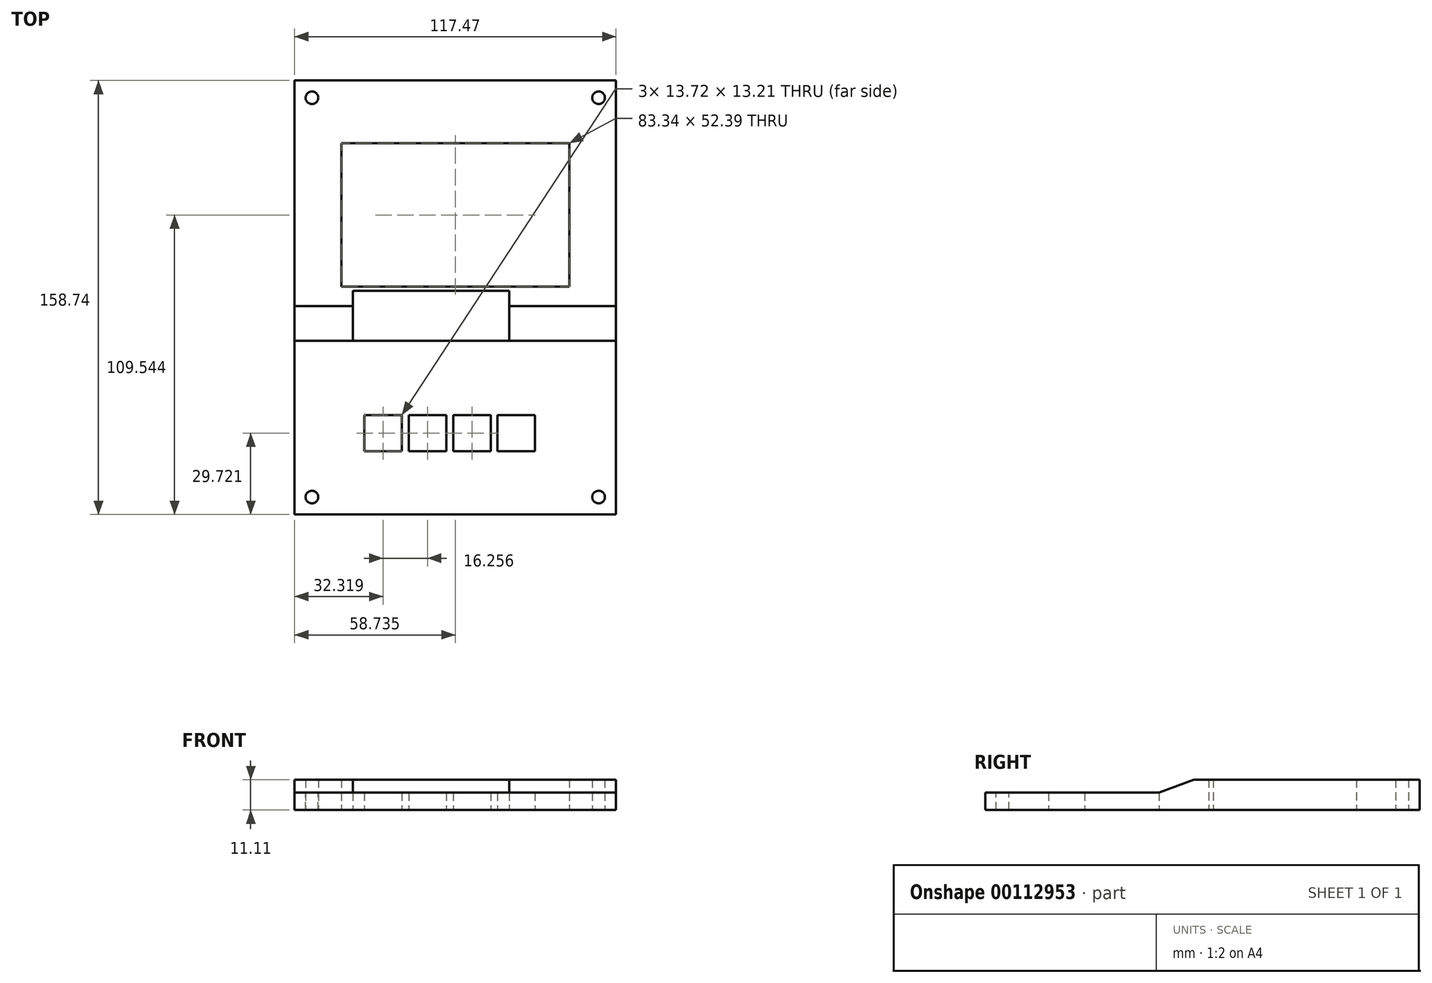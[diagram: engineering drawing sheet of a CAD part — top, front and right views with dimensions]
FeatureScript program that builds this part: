
annotation { "Feature Type Name" : "Feature", "Feature Type Description" : "" }
export const myFeature = defineFeature(function(context is Context, id is Id, definition is map)
    precondition{}
    {
        {
            var Q0;
            Q0=qCreatedBy(makeId("Top.planeOp"),FACE);
            var sketch = newSketch(context, id + "F0", { "sketchPlane" : qUnion([Q0])});
            skLineSegment(sketch, "E0.bottom", {"start": v(-61.75, 43.05) * mm, "end": v(30.32, 43.05) * mm});
            skLineSegment(sketch, "E0.top", {"start": v(-61.75, -26.8) * mm, "end": v(30.32, -26.8) * mm});
            skLineSegment(sketch, "E0.left", {"start": v(-61.75, 43.05) * mm, "end": v(-61.75, -26.8) * mm});
            skLineSegment(sketch, "E0.right", {"start": v(30.32, 43.05) * mm, "end": v(30.32, -26.8) * mm});
            skLineSegment(sketch, "E1", {"start": v(30.32, 43.05) * mm, "end": v(43.02, 43.05) * mm});
            skLineSegment(sketch, "E2", {"start": v(43.02, 43.05) * mm, "end": v(43.02, -26.8) * mm});
            skLineSegment(sketch, "E3", {"start": v(43.02, -26.8) * mm, "end": v(30.32, -26.8) * mm});
            skLineSegment(sketch, "E4", {"start": v(-61.75, 43.05) * mm, "end": v(-74.45, 43.05) * mm});
            skLineSegment(sketch, "E5", {"start": v(-74.45, 43.05) * mm, "end": v(-74.45, -26.8) * mm});
            skLineSegment(sketch, "E6", {"start": v(-74.45, -26.8) * mm, "end": v(-61.75, -26.8) * mm});
            skLineSegment(sketch, "E7", {"start": v(-74.45, 43.05) * mm, "end": v(-74.45, 55.73) * mm});
            skLineSegment(sketch, "E8", {"start": v(-74.45, 55.73) * mm, "end": v(43.02, 55.73) * mm});
            skLineSegment(sketch, "E9", {"start": v(43.02, 55.73) * mm, "end": v(43.02, 43.05) * mm});
            skLineSegment(sketch, "E10", {"start": v(-74.45, 55.73) * mm, "end": v(-68.1, 55.73) * mm});
            skLineSegment(sketch, "E11", {"start": v(-74.45, 55.73) * mm, "end": v(-74.45, 49.39) * mm});
            skCircle(sketch, "E12", {"center": v(-68.1, 49.39) * mm, "radius": 2.31 * mm});
            skLineSegment(sketch, "E13", {"start": v(43.02, 55.73) * mm, "end": v(36.67, 55.73) * mm});
            skLineSegment(sketch, "E14", {"start": v(36.67, 55.73) * mm, "end": v(43.02, 55.73) * mm});
            skCircle(sketch, "E15", {"center": v(36.67, 49.39) * mm, "radius": 2.31 * mm});
            skSolve(sketch);
        }
        {
            var Q0;
            Q0=makeQuery(id+"F0.imprint","IMPRINT",FACE,{"disambiguationData":[TD([[makeQuery(id+"F0.imprint","IMPRINT",EDGE,{"derivedFrom":sQuery(id+"F0.wireOp",EDGE,"E0.bottom")}),-1.0]])]});
            extrude(context, id + "F1", {"entities" : qUnion([Q0]), "depth" : 11.1 * mm});
        }
        {
            var Q0;
            Q0=makeQuery(id+"F1.opExtrude","CAP_FACE",FACE,{"disambiguationData":[OSD([sQuery(id+"F0.wireOp",EDGE,"E0.bottom"),sQuery(id+"F0.wireOp",EDGE,"E0.top"),sQuery(id+"F0.wireOp",EDGE,"E0.left"),sQuery(id+"F0.wireOp",EDGE,"E0.right")])],"isStart":true});
            var sketch = newSketch(context, id + "F2", { "sketchPlane" : qUnion([Q0])});
            skLineSegment(sketch, "E16.0.0", {"start": v(-35.27, 79.9) * mm, "end": v(-35.27, 71.25) * mm});
            skLineSegment(sketch, "E16.0.2", {"start": v(-48.99, 71.25) * mm, "end": v(-48.99, 79.9) * mm});
            skLineSegment(sketch, "E17.0.0", {"start": v(-19.02, 79.9) * mm, "end": v(-19.02, 71.25) * mm});
            skLineSegment(sketch, "E17.0.2", {"start": v(-32.73, 71.25) * mm, "end": v(-32.73, 79.9) * mm});
            skLineSegment(sketch, "E18.0.0", {"start": v(-2.76, 79.9) * mm, "end": v(-2.76, 71.25) * mm});
            skLineSegment(sketch, "E18.0.2", {"start": v(-16.48, 71.25) * mm, "end": v(-16.48, 79.9) * mm});
            skLineSegment(sketch, "E19.0.0", {"start": v(13.37, 79.9) * mm, "end": v(13.37, 71.25) * mm});
            skLineSegment(sketch, "E19.0.2", {"start": v(-0.35, 71.25) * mm, "end": v(-0.35, 79.9) * mm});
            skLineSegment(sketch, "E20.0.0", {"start": v(14.05, 39.5) * mm, "end": v(-61.75, 39.5) * mm});
            skLineSegment(sketch, "E20.0.1", {"start": v(-61.75, 39.5) * mm, "end": v(-61.75, 90.3) * mm});
            skLineSegment(sketch, "E20.0.2", {"start": v(-61.75, 90.3) * mm, "end": v(30.32, 90.3) * mm});
            skLineSegment(sketch, "E20.0.3", {"start": v(30.32, 90.3) * mm, "end": v(34.13, 81.24) * mm});
            skLineSegment(sketch, "E20.0.4", {"start": v(34.13, 81.24) * mm, "end": v(34.13, 39.5) * mm});
            skLineSegment(sketch, "E20.0.5", {"start": v(34.13, 39.5) * mm, "end": v(14.05, 39.5) * mm});
            skLineSegment(sketch, "E21.0.0", {"start": v(-49.05, 26.8) * mm, "end": v(-61.75, 26.8) * mm});
            skLineSegment(sketch, "E21.0.1", {"start": v(-61.75, 26.8) * mm, "end": v(-61.75, 39.5) * mm});
            skLineSegment(sketch, "E21.0.2", {"start": v(-61.75, 39.5) * mm, "end": v(14.05, 39.5) * mm});
            skLineSegment(sketch, "E21.0.3", {"start": v(14.05, 39.5) * mm, "end": v(34.13, 39.5) * mm});
            skLineSegment(sketch, "E21.0.4", {"start": v(34.13, 39.5) * mm, "end": v(34.13, 26.8) * mm});
            skLineSegment(sketch, "E21.0.5", {"start": v(34.13, 26.8) * mm, "end": v(27.78, 26.8) * mm});
            skLineSegment(sketch, "E21.0.6", {"start": v(27.78, 26.8) * mm, "end": v(3.96, 26.8) * mm});
            skLineSegment(sketch, "E21.0.7", {"start": v(3.96, 26.8) * mm, "end": v(-49.05, 26.8) * mm});
            skLineSegment(sketch, "E22.0.2", {"start": v(3.96, 26.8) * mm, "end": v(3.96, 21.25) * mm});
            skLineSegment(sketch, "E22.0.3", {"start": v(3.96, 21.25) * mm, "end": v(-45.24, 21.25) * mm});
            skLineSegment(sketch, "E23.0.0", {"start": v(23.97, -32.73) * mm, "end": v(-55.4, -32.73) * mm});
            skLineSegment(sketch, "E23.0.2", {"start": v(-55.4, 19.66) * mm, "end": v(23.97, 19.66) * mm});
            skLineSegment(sketch, "E24", {"start": v(3.96, 26.8) * mm, "end": v(3.96, 39.5) * mm});
            skLineSegment(sketch, "E25", {"start": v(-61.75, 90.3) * mm, "end": v(-61.75, 103) * mm});
            skLineSegment(sketch, "E26", {"start": v(30.32, 103) * mm, "end": v(30.32, 90.3) * mm});
            skLineSegment(sketch, "E27", {"start": v(-61.75, 103) * mm, "end": v(30.32, 103) * mm});
            skLineSegment(sketch, "E28", {"start": v(-57.38, -32.73) * mm, "end": v(25.95, -32.73) * mm});
            skLineSegment(sketch, "E29", {"start": v(-53.2, 26.8) * mm, "end": v(-53.2, 21.25) * mm});
            skLineSegment(sketch, "E30", {"start": v(-45.24, 21.25) * mm, "end": v(-53.2, 21.25) * mm});
            skLineSegment(sketch, "E31", {"start": v(-53.2, 26.8) * mm, "end": v(-53.2, 39.5) * mm});
            skLineSegment(sketch, "E32", {"start": v(-57.38, -32.73) * mm, "end": v(-57.38, 19.66) * mm});
            skLineSegment(sketch, "E33", {"start": v(-57.38, 19.66) * mm, "end": v(-55.4, 19.66) * mm});
            skLineSegment(sketch, "E34", {"start": v(25.95, -32.73) * mm, "end": v(25.95, 19.66) * mm});
            skLineSegment(sketch, "E35", {"start": v(25.95, 19.66) * mm, "end": v(23.97, 19.66) * mm});
            skLineSegment(sketch, "E36", {"start": v(24.63, 103) * mm, "end": v(24.63, 66.68) * mm});
            skLineSegment(sketch, "E37.bottom", {"start": v(-0.35, 66.68) * mm, "end": v(13.37, 66.68) * mm});
            skLineSegment(sketch, "E37.left", {"start": v(-0.35, 66.68) * mm, "end": v(-0.35, 79.9) * mm});
            skLineSegment(sketch, "E37.right", {"start": v(13.37, 66.68) * mm, "end": v(13.37, 79.9) * mm});
            skLineSegment(sketch, "E38.bottom", {"start": v(-16.48, 66.68) * mm, "end": v(-2.76, 66.68) * mm});
            skLineSegment(sketch, "E38.top", {"start": v(-16.48, 79.9) * mm, "end": v(-2.76, 79.9) * mm});
            skLineSegment(sketch, "E38.left", {"start": v(-16.48, 66.68) * mm, "end": v(-16.48, 79.9) * mm});
            skLineSegment(sketch, "E38.right", {"start": v(-2.76, 66.68) * mm, "end": v(-2.76, 79.9) * mm});
            skLineSegment(sketch, "E39.bottom", {"start": v(-32.73, 66.68) * mm, "end": v(-19.02, 66.68) * mm});
            skLineSegment(sketch, "E39.top", {"start": v(-32.73, 79.9) * mm, "end": v(-19.02, 79.9) * mm});
            skLineSegment(sketch, "E39.left", {"start": v(-32.73, 66.68) * mm, "end": v(-32.73, 79.9) * mm});
            skLineSegment(sketch, "E39.right", {"start": v(-19.02, 66.68) * mm, "end": v(-19.02, 79.9) * mm});
            skLineSegment(sketch, "E40.bottom", {"start": v(-48.99, 66.68) * mm, "end": v(-35.27, 66.68) * mm});
            skLineSegment(sketch, "E40.top", {"start": v(-48.99, 79.9) * mm, "end": v(-35.27, 79.9) * mm});
            skLineSegment(sketch, "E40.left", {"start": v(-48.99, 66.68) * mm, "end": v(-48.99, 79.9) * mm});
            skLineSegment(sketch, "E40.right", {"start": v(-35.27, 66.68) * mm, "end": v(-35.27, 79.9) * mm});
            skPoint(sketch, "E41.orphan", {"position": v(-35.27, 84.46) * mm});
            skPoint(sketch, "E42.orphan", {"position": v(-0.35, 84.46) * mm});
            skPoint(sketch, "E43.orphan", {"position": v(-2.76, 84.46) * mm});
            skPoint(sketch, "E44.orphan", {"position": v(13.37, 81.24) * mm});
            skLineSegment(sketch, "E45", {"start": v(-0.35, 79.9) * mm, "end": v(13.37, 79.9) * mm});
            skPoint(sketch, "E46.orphan", {"position": v(-48.99, 84.46) * mm});
            skLineSegment(sketch, "E47", {"start": v(-57.38, 21.28) * mm, "end": v(-53.2, 21.25) * mm});
            skSolve(sketch);
        }
        {
            var Q0;
            Q0=makeQuery(id+"F1.opExtrude","SWEPT_FACE",FACE,{"disambiguationData":[OSD([sQuery(id+"F0.wireOp",EDGE,"E0.left")])]});
            var sketch = newSketch(context, id + "F3", { "sketchPlane" : qUnion([Q0])});
            skLineSegment(sketch, "E48", {"start": v(26.8, 11.11) * mm, "end": v(26.8, 0) * mm});
            skPoint(sketch, "E49.end.orphan", {"position": v(52.2, 6.35) * mm});
            skPoint(sketch, "E50.end.orphan", {"position": v(52.2, 0) * mm});
            skLineSegment(sketch, "E51", {"start": v(39.5, 6.35) * mm, "end": v(26.8, 11.11) * mm});
            skLineSegment(sketch, "E52", {"start": v(39.5, 6.35) * mm, "end": v(39.5, 0) * mm});
            skLineSegment(sketch, "E53", {"start": v(39.5, 0) * mm, "end": v(26.8, 0) * mm});
            skSolve(sketch);
        }
        {
            var Q0;
            Q0=makeQuery(id+"F3.imprint","IMPRINT",FACE,{"disambiguationData":[TD([[makeQuery(id+"F3.imprint","IMPRINT",EDGE,{"derivedFrom":sQuery(id+"F3.wireOp",EDGE,"E48")}),1.0]])]});
            extrude(context, id + "F4", {"entities" : qUnion([Q0]), "operationType" : NewBodyOperationType.ADD, "oppositeDirection" : true, "depth" : 12.7 * mm});
        }
        {
            var Q0;
            Q0=makeQuery(id+"F1.opExtrude","SWEPT_FACE",FACE,{"disambiguationData":[OSD([sQuery(id+"F0.wireOp",EDGE,"E0.right")])]});
            var sketch = newSketch(context, id + "F5", { "sketchPlane" : qUnion([Q0])});
            skLineSegment(sketch, "E54", {"start": v(-26.8, 11.11) * mm, "end": v(-26.8, 0) * mm});
            skPoint(sketch, "E55.end.orphan", {"position": v(-52.2, 6.35) * mm});
            skPoint(sketch, "E55.start.orphan", {"position": v(-52.2, 0) * mm});
            skLineSegment(sketch, "E56", {"start": v(-39.5, 6.35) * mm, "end": v(-39.5, 0) * mm});
            skLineSegment(sketch, "E57", {"start": v(-39.5, 0) * mm, "end": v(-26.8, 0) * mm});
            skLineSegment(sketch, "E58", {"start": v(-39.5, 6.35) * mm, "end": v(-26.8, 11.11) * mm});
            skSolve(sketch);
        }
        {
            var Q0;
            Q0=makeQuery(id+"F5.imprint","IMPRINT",FACE,{"disambiguationData":[TD([[makeQuery(id+"F5.imprint","IMPRINT",EDGE,{"derivedFrom":sQuery(id+"F5.wireOp",EDGE,"E54")}),-1.0]])]});
            extrude(context, id + "F6", {"entities" : qUnion([Q0]), "operationType" : NewBodyOperationType.ADD, "oppositeDirection" : true, "depth" : 30.18 * mm});
        }
        {
            var Q0;
            Q0=makeQuery(id+"F0.imprint","IMPRINT",FACE,{"disambiguationData":[TD([[makeQuery(id+"F0.imprint","IMPRINT",EDGE,{"derivedFrom":sQuery(id+"F0.wireOp",EDGE,"E0.left")}),-1.0]])]});
            var Q1;
            Q1=makeQuery(id+"F0.imprint","IMPRINT",FACE,{"disambiguationData":[TD([[makeQuery(id+"F0.imprint","IMPRINT",EDGE,{"derivedFrom":sQuery(id+"F0.wireOp",EDGE,"E0.right")}),1.0]])]});
            var Q2;
            Q2=makeQuery(id+"F0.imprint","IMPRINT",FACE,{"disambiguationData":[TD([[makeQuery(id+"F0.imprint","IMPRINT",EDGE,{"derivedFrom":sQuery(id+"F0.wireOp",EDGE,"E0.bottom")}),1.0]])]});
            extrude(context, id + "F7", {"entities" : qUnion([Q0, Q1, Q2]), "operationType" : NewBodyOperationType.ADD, "depth" : 11.1 * mm});
        }
        {
            var Q0;
            Q0=makeQuery(id+"F5.imprint","IMPRINT",FACE,{"disambiguationData":[TD([[makeQuery(id+"F5.imprint","IMPRINT",EDGE,{"derivedFrom":sQuery(id+"F5.wireOp",EDGE,"E54")}),-1.0]])]});
            extrude(context, id + "F8", {"entities" : qUnion([Q0]), "operationType" : NewBodyOperationType.ADD, "depth" : 12.7 * mm});
        }
        {
            var Q0;
            Q0=makeQuery(id+"F3.imprint","IMPRINT",FACE,{"disambiguationData":[TD([[makeQuery(id+"F3.imprint","IMPRINT",EDGE,{"derivedFrom":sQuery(id+"F3.wireOp",EDGE,"E48")}),1.0]])]});
            extrude(context, id + "F9", {"entities" : qUnion([Q0]), "operationType" : NewBodyOperationType.ADD, "depth" : 12.7 * mm});
        }
        {
            var Q0;
            Q0=makeQuery(id+"F9.opExtrude","SWEPT_FACE",FACE,{"disambiguationData":[OSD([sQuery(id+"F3.wireOp",EDGE,"E52")])]});
            var Q1;
            Q1=makeQuery(id+"F8.opExtrude","SWEPT_FACE",FACE,{"disambiguationData":[OSD([sQuery(id+"F5.wireOp",EDGE,"E56")])]});
            extrude(context, id + "F10", {"entities" : qUnion([Q0, Q1]), "operationType" : NewBodyOperationType.ADD, "depth" : 50.8 * mm});
        }
        {
            var Q0;
            Q0=makeQuery(id+"F2.imprint","IMPRINT",FACE,{"disambiguationData":[TD([[makeQuery(id+"F2.imprint","IMPRINT",EDGE,{"derivedFrom":sQuery(id+"F2.wireOp",EDGE,"E20.0.2")}),1.0]])]});
            extrude(context, id + "F11", {"entities" : qUnion([Q0]), "operationType" : NewBodyOperationType.ADD, "oppositeDirection" : true, "depth" : 6.35 * mm});
        }
        {
            var Q0;
            Q0=makeQuery(id+"F11.opExtrude","SWEPT_FACE",FACE,{"disambiguationData":[OSD([sQuery(id+"F2.wireOp",EDGE,"E25")])]});
            extrude(context, id + "F12", {"entities" : qUnion([Q0]), "operationType" : NewBodyOperationType.ADD, "depth" : 12.7 * mm});
        }
        {
            var Q0;
            Q0=makeQuery(id+"F11.opExtrude","SWEPT_FACE",FACE,{"disambiguationData":[OSD([sQuery(id+"F2.wireOp",EDGE,"E26")])]});
            extrude(context, id + "F13", {"entities" : qUnion([Q0]), "operationType" : NewBodyOperationType.ADD, "depth" : 12.7 * mm});
        }
        {
            var Q0;
            {var subQ0=sQuery(id+"F2.wireOp",EDGE,"E26");var subQ1=sQuery(id+"F2.wireOp",EDGE,"E25");var subQ2=sQuery(id+"F2.wireOp",EDGE,"E20.0.2");Q0=makeQuery(id+"F13.boolean.opBoolean","MERGE",FACE,{"derivedFrom":[makeQuery(id+"F12.boolean.opBoolean","MERGE",FACE,{"derivedFrom":[makeQuery(id+"F11.boolean.opBoolean","MERGE",FACE,{"derivedFrom":[makeQuery(id+"Fx8EoAPbX89bgpt_1.opExtrude","CAP_FACE",FACE,{"disambiguationData":[OSD([sQuery(id+"F2.wireOp",EDGE,"E16.0.0"),sQuery(id+"F2.wireOp",EDGE,"E16.0.1"),sQuery(id+"F2.wireOp",EDGE,"E16.0.2"),sQuery(id+"F2.wireOp",EDGE,"E16.0.3"),sQuery(id+"F2.wireOp",EDGE,"E17.0.0"),sQuery(id+"F2.wireOp",EDGE,"E17.0.1"),sQuery(id+"F2.wireOp",EDGE,"E17.0.2"),sQuery(id+"F2.wireOp",EDGE,"E17.0.3"),sQuery(id+"F2.wireOp",EDGE,"E18.0.0"),sQuery(id+"F2.wireOp",EDGE,"E18.0.1"),sQuery(id+"F2.wireOp",EDGE,"E18.0.2"),sQuery(id+"F2.wireOp",EDGE,"E18.0.3"),sQuery(id+"F2.wireOp",EDGE,"E19.0.0"),sQuery(id+"F2.wireOp",EDGE,"E19.0.1"),sQuery(id+"F2.wireOp",EDGE,"E19.0.2"),sQuery(id+"F2.wireOp",EDGE,"E19.0.3"),sQuery(id+"F2.wireOp",EDGE,"E19.0.4"),sQuery(id+"F2.wireOp",EDGE,"E20.0.1"),subQ2,sQuery(id+"F2.wireOp",EDGE,"E20.0.3"),sQuery(id+"F2.wireOp",EDGE,"E20.0.4"),sQuery(id+"F2.wireOp",EDGE,"E21.0.2"),sQuery(id+"F2.wireOp",EDGE,"E21.0.3")])],"isStart":false}),makeQuery(id+"F11.opExtrude","CAP_FACE",FACE,{"disambiguationData":[OSD([subQ2,subQ1,subQ0,sQuery(id+"F2.wireOp",EDGE,"E27")])],"isStart":false})]}),makeQuery(id+"F12.opExtrude","SWEPT_FACE",FACE,{"disambiguationData":[OSD([subQ1]),TDD([makeQuery(id+"F11.opExtrude","CAP_EDGE",EDGE,{"disambiguationData":[OSD([subQ1])],"isStart":false})])]})]}),makeQuery(id+"F13.opExtrude","SWEPT_FACE",FACE,{"disambiguationData":[OSD([subQ0]),TDD([makeQuery(id+"F11.opExtrude","CAP_EDGE",EDGE,{"disambiguationData":[OSD([subQ0])],"isStart":false})])]})]});}
            var sketch = newSketch(context, id + "F14", { "sketchPlane" : qUnion([Q0])});
            skLineSegment(sketch, "E59", {"start": v(-74.45, -103) * mm, "end": v(-68.1, -103) * mm});
            skLineSegment(sketch, "E60", {"start": v(-74.45, -103) * mm, "end": v(-74.45, -96.65) * mm});
            skLineSegment(sketch, "E61", {"start": v(43.02, -103) * mm, "end": v(36.67, -103) * mm});
            skLineSegment(sketch, "E62", {"start": v(43.02, -103) * mm, "end": v(43.02, -96.65) * mm});
            skCircle(sketch, "E63", {"center": v(-68.1, -96.65) * mm, "radius": 2.31 * mm});
            skCircle(sketch, "E64", {"center": v(36.67, -96.65) * mm, "radius": 2.31 * mm});
            skSolve(sketch);
        }
        {
            var Q0;
            Q0=makeQuery(id+"F14.imprint","IMPRINT",FACE,{"disambiguationData":[TD([[makeQuery(id+"F14.imprint","IMPRINT",EDGE,{"derivedFrom":sQuery(id+"F14.wireOp",EDGE,"E63")}),1.0]])]});
            var Q1;
            Q1=makeQuery(id+"F14.imprint","IMPRINT",FACE,{"disambiguationData":[TD([[makeQuery(id+"F14.imprint","IMPRINT",EDGE,{"derivedFrom":sQuery(id+"F14.wireOp",EDGE,"E64")}),1.0]])]});
            extrude(context, id + "F15", {"entities" : qUnion([Q0, Q1]), "operationType" : NewBodyOperationType.REMOVE, "oppositeDirection" : true, "depth" : 6.35 * mm});
        }
        {
            var Q0;
            Q0=makeQuery(id+"F2.imprint","IMPRINT",FACE,{"disambiguationData":[TD([[makeQuery(id+"F2.imprint","IMPRINT",EDGE,{"derivedFrom":sQuery(id+"F2.wireOp",EDGE,"E23.0.2")}),-1.0]])]});
            extrude(context, id + "F16", {"entities" : qUnion([Q0]), "operationType" : NewBodyOperationType.REMOVE, "oppositeDirection" : true, "depth" : 11.1 * mm});
        }
        {
            var Q0;
            {var subQ0=sQuery(id+"F2.wireOp",EDGE,"E21.0.7");Q0=makeQuery(id+"F2.imprint","IMPRINT",FACE,{"disambiguationData":[TD([[makeQuery(id+"F2.imprint","IMPRINT",EDGE,{"derivedFrom":subQ0}),1.0]])]});}
            var Q1;
            {var subQ0=sQuery(id+"F2.wireOp",EDGE,"E21.0.7");Q1=makeQuery(id+"F2.imprint","IMPRINT",FACE,{"disambiguationData":[TD([[makeQuery(id+"F2.imprint","IMPRINT",EDGE,{"derivedFrom":subQ0}),-1.0]])]});}
            extrude(context, id + "F17", {"entities" : qUnion([Q0, Q1]), "operationType" : NewBodyOperationType.REMOVE, "oppositeDirection" : true, "depth" : 11.1 * mm});
        }
        {
            var Q0;
            {var subQ23=sQuery(id+"F2.wireOp",EDGE,"E20.0.1");Q0=makeQuery(id+"F2.imprint","IMPRINT",FACE,{"disambiguationData":[TD([[makeQuery(id+"F2.imprint","IMPRINT",EDGE,{"derivedFrom":subQ23}),-1.0]])]});}
            extrude(context, id + "F18", {"entities" : qUnion([Q0]), "operationType" : NewBodyOperationType.ADD, "oppositeDirection" : true, "depth" : 6.35 * mm});
        }
        {
            var Q0;
            {var subQ1=sQuery(id+"F2.wireOp",EDGE,"E37.bottom");Q0=makeQuery(id+"F2.imprint","IMPRINT",FACE,{"disambiguationData":[TD([[makeQuery(id+"F2.imprint","IMPRINT",EDGE,{"derivedFrom":subQ1}),1.0]])]});}
            extrude(context, id + "F19", {"entities" : qUnion([Q0]), "operationType" : NewBodyOperationType.REMOVE, "oppositeDirection" : true, "depth" : 6.35 * mm});
        }
    });
